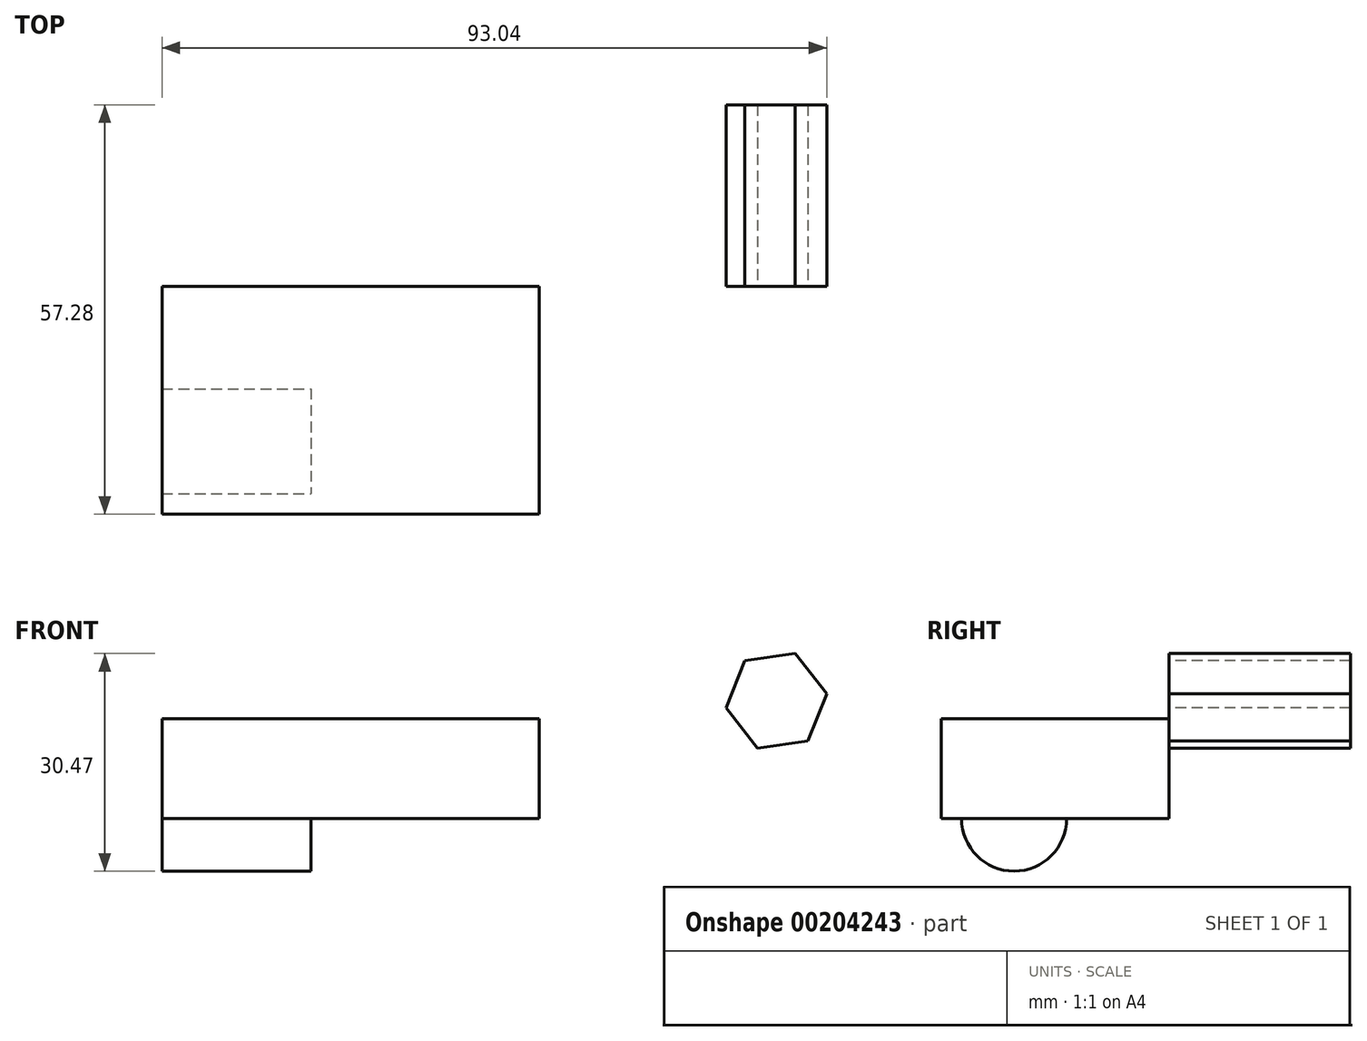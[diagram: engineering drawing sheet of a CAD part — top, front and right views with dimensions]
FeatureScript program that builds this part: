
annotation { "Feature Type Name" : "Feature", "Feature Type Description" : "" }
export const myFeature = defineFeature(function(context is Context, id is Id, definition is map)
    precondition{}
    {
        {
            var Q0;
            Q0=qCreatedBy(makeId("Top.planeOp"),FACE);
            var sketch = newSketch(context, id + "F0", { "sketchPlane" : qUnion([Q0])});
            skLineSegment(sketch, "E0.bottom", {"start": v(-7.77, -15.94) * mm, "end": v(-50.13, -15.94) * mm});
            skLineSegment(sketch, "E0.top", {"start": v(-7.77, 15.94) * mm, "end": v(-50.13, 15.94) * mm});
            skLineSegment(sketch, "E0.left", {"start": v(-7.77, -15.94) * mm, "end": v(-7.77, 15.94) * mm});
            skLineSegment(sketch, "E0.right", {"start": v(-50.13, -15.94) * mm, "end": v(-50.13, 15.94) * mm});
            skPoint(sketch, "E0.middle", {"position": v(-28.95, 0) * mm});
            skSolve(sketch);
        }
        {
            var Q0;
            Q0 = qSketchRegion(id + "F0", true);
            extrude(context, id + "F1", {"entities" : qUnion([Q0]), "endBound" : BoundingType.SYMMETRIC, "depth" : 14 * mm});
        }
        {
            var Q0;
            Q0=makeQuery(id+"F1.opExtrude","SWEPT_FACE",FACE,{"disambiguationData":[OSD([sQuery(id+"F0.wireOp",EDGE,"E0.right")])]});
            var sketch = newSketch(context, id + "F2", { "sketchPlane" : qUnion([Q0])});
            skCircle(sketch, "E1", {"center": v(5.73, -7) * mm, "radius": 7.35 * mm});
            skSolve(sketch);
        }
        {
            var Q0;
            {var subQ0=sQuery(id+"F2.wireOp",EDGE,"E1");var subQ1=makeQuery(id+"F1.opExtrude","CAP_EDGE",EDGE,{"disambiguationData":[OSD([sQuery(id+"F0.wireOp",EDGE,"E0.right")])],"isStart":true});var subQ2=makeQuery(id+"F2.imprint","INTERSECT",VERTEX,{"disambiguationData":[OD(0.0)],"derivedFrom":[subQ1,subQ0]});Q0=makeQuery(id+"F2.imprint","IMPRINT",FACE,{"disambiguationData":[TD([[makeQuery(id+"F2.imprint","IMPRINT",EDGE,{"disambiguationData":[TD([[subQ2,-1.0]])],"derivedFrom":subQ0}),1.0]])]});}
            var Q1;
            Q1=makeQuery(id+"F1.opExtrude","SWEPT_FACE",FACE,{"disambiguationData":[OSD([sQuery(id+"F0.wireOp",EDGE,"E0.right")])]});
            var Q2;
            {var subQ0=sQuery(id+"F2.wireOp",EDGE,"E1");var subQ1=makeQuery(id+"F1.opExtrude","CAP_EDGE",EDGE,{"disambiguationData":[OSD([sQuery(id+"F0.wireOp",EDGE,"E0.right")])],"isStart":true});var subQ2=makeQuery(id+"F2.imprint","INTERSECT",VERTEX,{"disambiguationData":[OD(0.0)],"derivedFrom":[subQ1,subQ0]});Q2=makeQuery(id+"F2.imprint","IMPRINT",FACE,{"disambiguationData":[TD([[makeQuery(id+"F2.imprint","IMPRINT",EDGE,{"disambiguationData":[TD([[subQ2,1.0]])],"derivedFrom":subQ0}),1.0]])]});}
            extrude(context, id + "F3", {"entities" : qUnion([Q0, Q1, Q2]), "operationType" : NewBodyOperationType.ADD, "endBound" : BoundingType.SYMMETRIC, "depth" : 20.83 * mm});
        }
        {
            var Q0;
            {var subQ0=sQuery(id+"F0.wireOp",EDGE,"E0.top");Q0=makeQuery(id+"F3.boolean.opBoolean","MERGE",FACE,{"derivedFrom":[makeQuery(id+"F1.opExtrude","SWEPT_FACE",FACE,{"disambiguationData":[OSD([subQ0])]}),makeQuery(id+"F3.opExtrude","SWEPT_FACE",FACE,{"disambiguationData":[OSD([subQ0,sQuery(id+"F0.wireOp",EDGE,"E0.right")])]})]});}
            var sketch = newSketch(context, id + "F4", { "sketchPlane" : qUnion([Q0])});
            skCircle(sketch, "E2.cCircle", {"center": v(-25.43, 9.5) * mm, "radius": 7.13 * mm, "construction": true});
            skLineSegment(sketch, "E2.0", {"start": v(-28.09, 16.12) * mm, "end": v(-21.03, 15.1) * mm});
            skLineSegment(sketch, "E2.1", {"start": v(-21.03, 15.1) * mm, "end": v(-18.37, 8.49) * mm});
            skLineSegment(sketch, "E2.2", {"start": v(-18.37, 8.49) * mm, "end": v(-22.78, 2.88) * mm});
            skLineSegment(sketch, "E2.3", {"start": v(-22.78, 2.88) * mm, "end": v(-29.84, 3.9) * mm});
            skLineSegment(sketch, "E2.4", {"start": v(-29.84, 3.9) * mm, "end": v(-32.5, 10.51) * mm});
            skLineSegment(sketch, "E2.5", {"start": v(-32.5, 10.51) * mm, "end": v(-28.09, 16.12) * mm});
            skCircle(sketch, "E3.cCircle", {"center": v(-20.02, 9.67) * mm, "radius": 23.24 * mm, "construction": true});
            skLineSegment(sketch, "E3.0", {"start": v(0, 21.48) * mm, "end": v(-8.21, -10.34) * mm});
            skLineSegment(sketch, "E3.1", {"start": v(-8.21, -10.34) * mm, "end": v(-40.04, -2.13) * mm});
            skLineSegment(sketch, "E3.3", {"start": v(-31.82, 29.7) * mm, "end": v(0, 21.48) * mm});
            skSolve(sketch);
        }
        {
            var Q0;
            Q0 = qSketchRegion(id + "F4", true);
            extrude(context, id + "F5", {"entities" : qUnion([Q0]), "depth" : 25.4 * mm});
        }
    });
